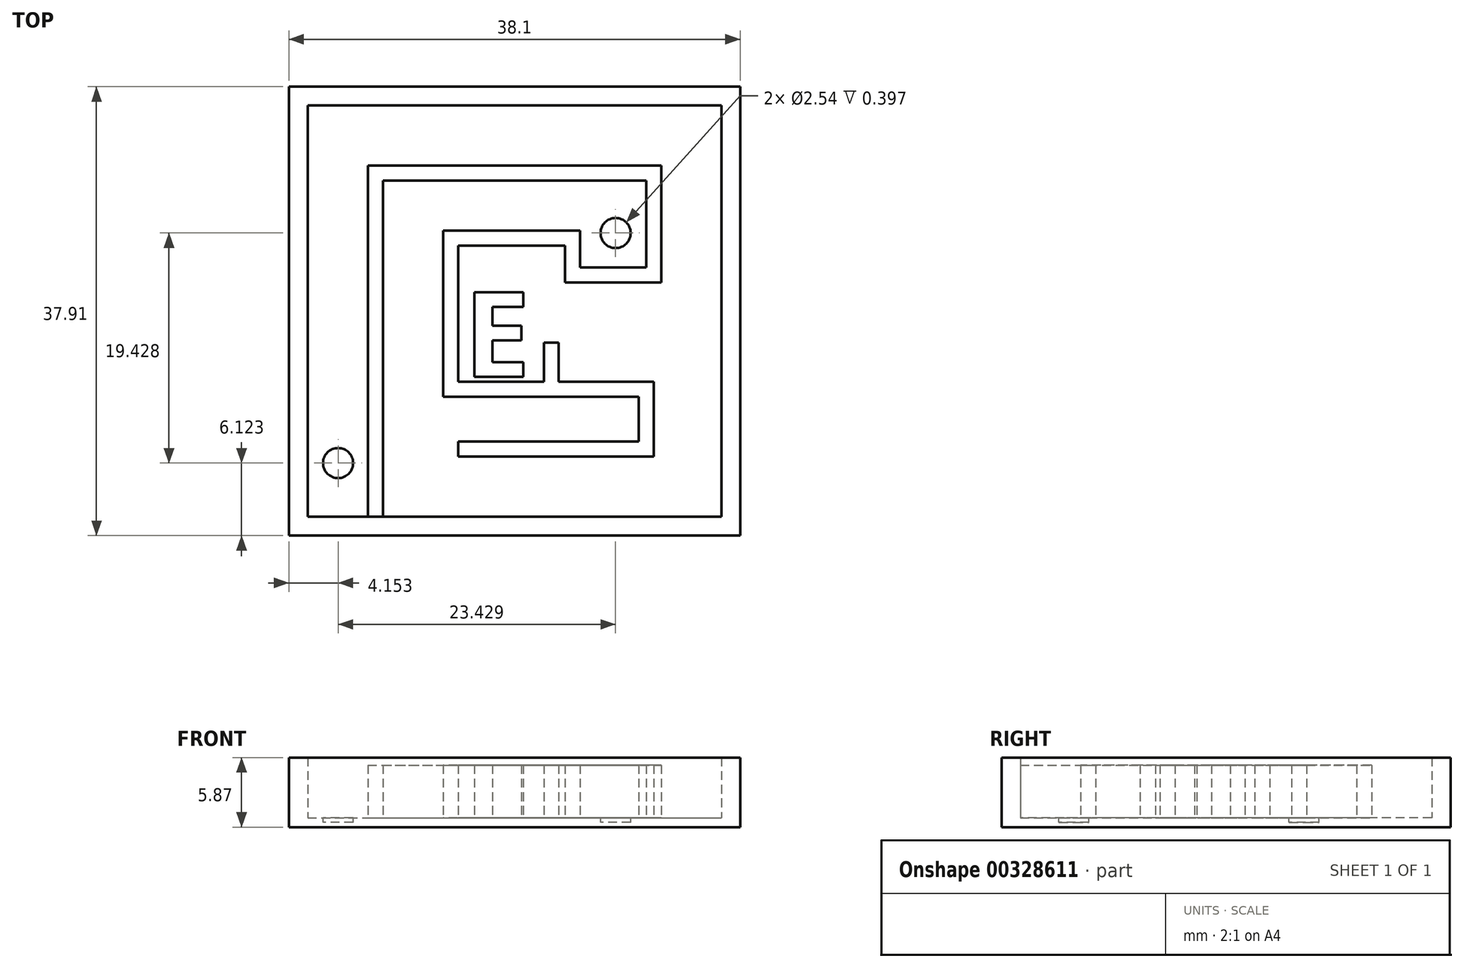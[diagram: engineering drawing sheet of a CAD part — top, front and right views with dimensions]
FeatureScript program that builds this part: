
annotation { "Feature Type Name" : "Feature", "Feature Type Description" : "" }
export const myFeature = defineFeature(function(context is Context, id is Id, definition is map)
    precondition{}
    {
        {
            var Q0;
            Q0=qCreatedBy(makeId("Top.planeOp"),FACE);
            var sketch = newSketch(context, id + "F0", { "sketchPlane" : qUnion([Q0])});
            skLineSegment(sketch, "E0.bottom", {"start": v(-68.11, 13.4) * mm, "end": v(-30.01, 13.4) * mm});
            skLineSegment(sketch, "E0.top", {"start": v(-68.11, -24.52) * mm, "end": v(-30.01, -24.52) * mm});
            skLineSegment(sketch, "E0.left", {"start": v(-68.11, 13.4) * mm, "end": v(-68.11, -24.52) * mm});
            skLineSegment(sketch, "E0.right", {"start": v(-30.01, 13.4) * mm, "end": v(-30.01, -24.52) * mm});
            skSolve(sketch);
        }
        {
            var Q0;
            Q0=makeQuery(id+"F0.imprint","IMPRINT",FACE,{"disambiguationData":[TD([[makeQuery(id+"F0.imprint","IMPRINT",EDGE,{"derivedFrom":sQuery(id+"F0.wireOp",EDGE,"E0.bottom")}),-1.0]])]});
            extrude(context, id + "F1", {"entities" : qUnion([Q0]), "depth" : 0.8 * mm});
        }
        {
            var Q0;
            Q0=makeQuery(id+"F1.opExtrude","CAP_FACE",FACE,{"disambiguationData":[OSD([sQuery(id+"F0.wireOp",EDGE,"E0.bottom"),sQuery(id+"F0.wireOp",EDGE,"E0.top"),sQuery(id+"F0.wireOp",EDGE,"E0.left"),sQuery(id+"F0.wireOp",EDGE,"E0.right")])],"isStart":false});
            var sketch = newSketch(context, id + "F2", { "sketchPlane" : qUnion([Q0])});
            skLineSegment(sketch, "E1.0", {"start": v(-66.52, 11.8) * mm, "end": v(-31.6, 11.8) * mm});
            skLineSegment(sketch, "E1.1", {"start": v(-66.52, 11.8) * mm, "end": v(-66.52, -22.93) * mm});
            skLineSegment(sketch, "E1.2", {"start": v(-66.52, -22.93) * mm, "end": v(-31.6, -22.93) * mm});
            skLineSegment(sketch, "E1.3", {"start": v(-31.6, 11.8) * mm, "end": v(-31.6, -22.93) * mm});
            skSolve(sketch);
        }
        {
            var Q0;
            Q0=makeQuery(id+"F2.imprint","IMPRINT",FACE,{"disambiguationData":[TD([[makeQuery(id+"F2.imprint","IMPRINT",EDGE,{"derivedFrom":sQuery(id+"F2.wireOp",EDGE,"E1.0")}),1.0]])]});
            extrude(context, id + "F3", {"entities" : qUnion([Q0]), "operationType" : NewBodyOperationType.ADD, "depth" : 5.08 * mm});
        }
        {
            var Q0;
            Q0=makeQuery(id+"F1.opExtrude","CAP_FACE",FACE,{"disambiguationData":[OSD([sQuery(id+"F0.wireOp",EDGE,"E0.bottom"),sQuery(id+"F0.wireOp",EDGE,"E0.top"),sQuery(id+"F0.wireOp",EDGE,"E0.left"),sQuery(id+"F0.wireOp",EDGE,"E0.right")])],"isStart":false});
            var sketch = newSketch(context, id + "F4", { "sketchPlane" : qUnion([Q0])});
            skLineSegment(sketch, "E2.bottom", {"start": v(-61.44, -22.93) * mm, "end": v(-60.17, -22.93) * mm});
            skLineSegment(sketch, "E2.top", {"start": v(-61.44, 6.72) * mm, "end": v(-60.17, 6.72) * mm});
            skLineSegment(sketch, "E2.left", {"start": v(-61.44, -22.93) * mm, "end": v(-61.44, 6.72) * mm});
            skLineSegment(sketch, "E2.right", {"start": v(-60.17, -22.93) * mm, "end": v(-60.17, 5.45) * mm});
            skLineSegment(sketch, "E3.bottom", {"start": v(-60.17, 6.72) * mm, "end": v(-37.95, 6.72) * mm});
            skLineSegment(sketch, "E3.top", {"start": v(-60.17, 5.45) * mm, "end": v(-37.95, 5.45) * mm});
            skLineSegment(sketch, "E4.bottom", {"start": v(-37.95, 6.72) * mm, "end": v(-36.68, 6.72) * mm});
            skLineSegment(sketch, "E4.top", {"start": v(-37.95, -3.15) * mm, "end": v(-36.68, -3.15) * mm});
            skLineSegment(sketch, "E4.left", {"start": v(-37.95, 5.45) * mm, "end": v(-37.95, -1.88) * mm});
            skLineSegment(sketch, "E4.right", {"start": v(-36.68, 6.72) * mm, "end": v(-36.68, -3.15) * mm});
            skLineSegment(sketch, "E5.bottom", {"start": v(-37.95, -3.15) * mm, "end": v(-43.51, -3.15) * mm});
            skLineSegment(sketch, "E5.top", {"start": v(-37.95, -1.88) * mm, "end": v(-43.51, -1.88) * mm});
            skLineSegment(sketch, "E6.bottom", {"start": v(-43.51, -3.15) * mm, "end": v(-44.78, -3.15) * mm});
            skLineSegment(sketch, "E6.top", {"start": v(-43.51, 1.24) * mm, "end": v(-44.78, 1.24) * mm});
            skLineSegment(sketch, "E6.left", {"start": v(-43.51, -1.88) * mm, "end": v(-43.51, 1.24) * mm});
            skLineSegment(sketch, "E6.right", {"start": v(-44.78, -3.15) * mm, "end": v(-44.78, -0.03) * mm});
            skLineSegment(sketch, "E7.bottom", {"start": v(-44.78, 1.24) * mm, "end": v(-55.1, 1.24) * mm});
            skLineSegment(sketch, "E7.top", {"start": v(-44.78, -0.03) * mm, "end": v(-53.82, -0.03) * mm});
            skLineSegment(sketch, "E7.right", {"start": v(-55.1, 1.24) * mm, "end": v(-55.1, -0.03) * mm});
            skLineSegment(sketch, "E8.left", {"start": v(-55.1, -0.03) * mm, "end": v(-55.1, -11.54) * mm});
            skLineSegment(sketch, "E8.right", {"start": v(-53.82, -0.03) * mm, "end": v(-53.82, -11.54) * mm});
            skLineSegment(sketch, "E9.bottom", {"start": v(-53.82, -11.54) * mm, "end": v(-46.6, -11.54) * mm});
            skLineSegment(sketch, "E9.top", {"start": v(-55.1, -12.8) * mm, "end": v(-48.6, -12.8) * mm});
            skLineSegment(sketch, "E9.left", {"start": v(-55.1, -11.54) * mm, "end": v(-55.1, -12.8) * mm});
            skLineSegment(sketch, "E10.left", {"start": v(-45.32, -11.54) * mm, "end": v(-45.32, -8.23) * mm});
            skLineSegment(sketch, "E10.right", {"start": v(-46.6, -11.54) * mm, "end": v(-46.6, -8.23) * mm});
            skPoint(sketch, "E11.oppositeSnap0", {"position": v(-37.31, -3.15) * mm});
            skLineSegment(sketch, "E11.bottom", {"start": v(-45.32, -11.54) * mm, "end": v(-37.31, -11.54) * mm});
            skLineSegment(sketch, "E11.top", {"start": v(-48.6, -12.8) * mm, "end": v(-38.58, -12.8) * mm});
            skLineSegment(sketch, "E11.right", {"start": v(-37.31, -11.54) * mm, "end": v(-37.31, -12.8) * mm});
            skLineSegment(sketch, "E12.top", {"start": v(-37.31, -17.85) * mm, "end": v(-38.58, -17.85) * mm});
            skLineSegment(sketch, "E12.left", {"start": v(-37.31, -12.8) * mm, "end": v(-37.31, -17.85) * mm});
            skLineSegment(sketch, "E12.right", {"start": v(-38.58, -12.8) * mm, "end": v(-38.58, -16.58) * mm});
            skLineSegment(sketch, "E13.bottom", {"start": v(-38.58, -17.85) * mm, "end": v(-53.82, -17.85) * mm});
            skLineSegment(sketch, "E13.top", {"start": v(-38.58, -16.58) * mm, "end": v(-53.82, -16.58) * mm});
            skLineSegment(sketch, "E13.right", {"start": v(-53.82, -17.85) * mm, "end": v(-53.82, -16.58) * mm});
            skLineSegment(sketch, "E14", {"start": v(-46.6, -8.23) * mm, "end": v(-45.32, -8.23) * mm});
            skSolve(sketch);
        }
        {
            var Q0;
            Q0=makeQuery(id+"F4.imprint","IMPRINT",FACE,{"disambiguationData":[TD([[makeQuery(id+"F4.imprint","IMPRINT",EDGE,{"derivedFrom":sQuery(id+"F4.wireOp",EDGE,"E2.top")}),1.0]])]});
            var sketch = newSketch(context, id + "F5", { "sketchPlane" : qUnion([Q0])});
            skCircle(sketch, "E15", {"center": v(-63.96, -18.4) * mm, "radius": 1.27 * mm});
            skSolve(sketch);
        }
        {
            var Q0;
            Q0=makeQuery(id+"F4.imprint","IMPRINT",FACE,{"disambiguationData":[TD([[makeQuery(id+"F4.imprint","IMPRINT",EDGE,{"derivedFrom":sQuery(id+"F4.wireOp",EDGE,"E2.top")}),1.0]])]});
            var sketch = newSketch(context, id + "F6", { "sketchPlane" : qUnion([Q0])});
            skCircle(sketch, "E16", {"center": v(-40.53, 1.03) * mm, "radius": 1.27 * mm});
            skSolve(sketch);
        }
        {
            var Q0;
            Q0=makeQuery(id+"F4.imprint","IMPRINT",FACE,{"disambiguationData":[TD([[makeQuery(id+"F4.imprint","IMPRINT",EDGE,{"derivedFrom":sQuery(id+"F4.wireOp",EDGE,"E2.bottom")}),1.0]])]});
            extrude(context, id + "F7", {"entities" : qUnion([Q0]), "operationType" : NewBodyOperationType.ADD, "depth" : 4.44 * mm});
        }
        {
            var Q0;
            Q0=makeQuery(id+"F5.imprint","IMPRINT",FACE,{"disambiguationData":[TD([[makeQuery(id+"F5.imprint","IMPRINT",EDGE,{"derivedFrom":sQuery(id+"F5.wireOp",EDGE,"E15")}),-1.0]])]});
            var sketch = newSketch(context, id + "F8", { "sketchPlane" : qUnion([Q0])});
            skText(sketch, "E17", { "text": "E", "fontName": "OpenSans-Bold.ttf"});
            const initialGuessF8  = {"E17": [-0.05334, -0.01113, 1, 0, 0.00722]};
            skSetInitialGuess(sketch, initialGuessF8);
            skSolve(sketch);
        }
        {
            var Q0;
            Q0 = qSketchRegion(id + "F8", true);
            extrude(context, id + "F9", {"entities" : qUnion([Q0]), "operationType" : NewBodyOperationType.ADD, "depth" : 4.44 * mm});
        }
        {
            var Q0;
            Q0=makeQuery(id+"F5.imprint","IMPRINT",FACE,{"disambiguationData":[TD([[makeQuery(id+"F5.imprint","IMPRINT",EDGE,{"derivedFrom":sQuery(id+"F5.wireOp",EDGE,"E15")}),1.0]])]});
            extrude(context, id + "F10", {"entities" : qUnion([Q0]), "operationType" : NewBodyOperationType.REMOVE, "oppositeDirection" : true, "depth" : 0.4 * mm});
        }
        {
            var Q0;
            Q0=makeQuery(id+"F6.imprint","IMPRINT",FACE,{"disambiguationData":[TD([[makeQuery(id+"F6.imprint","IMPRINT",EDGE,{"derivedFrom":sQuery(id+"F6.wireOp",EDGE,"E16")}),1.0]])]});
            extrude(context, id + "F11", {"entities" : qUnion([Q0]), "operationType" : NewBodyOperationType.REMOVE, "oppositeDirection" : true, "depth" : 0.4 * mm});
        }
    });
